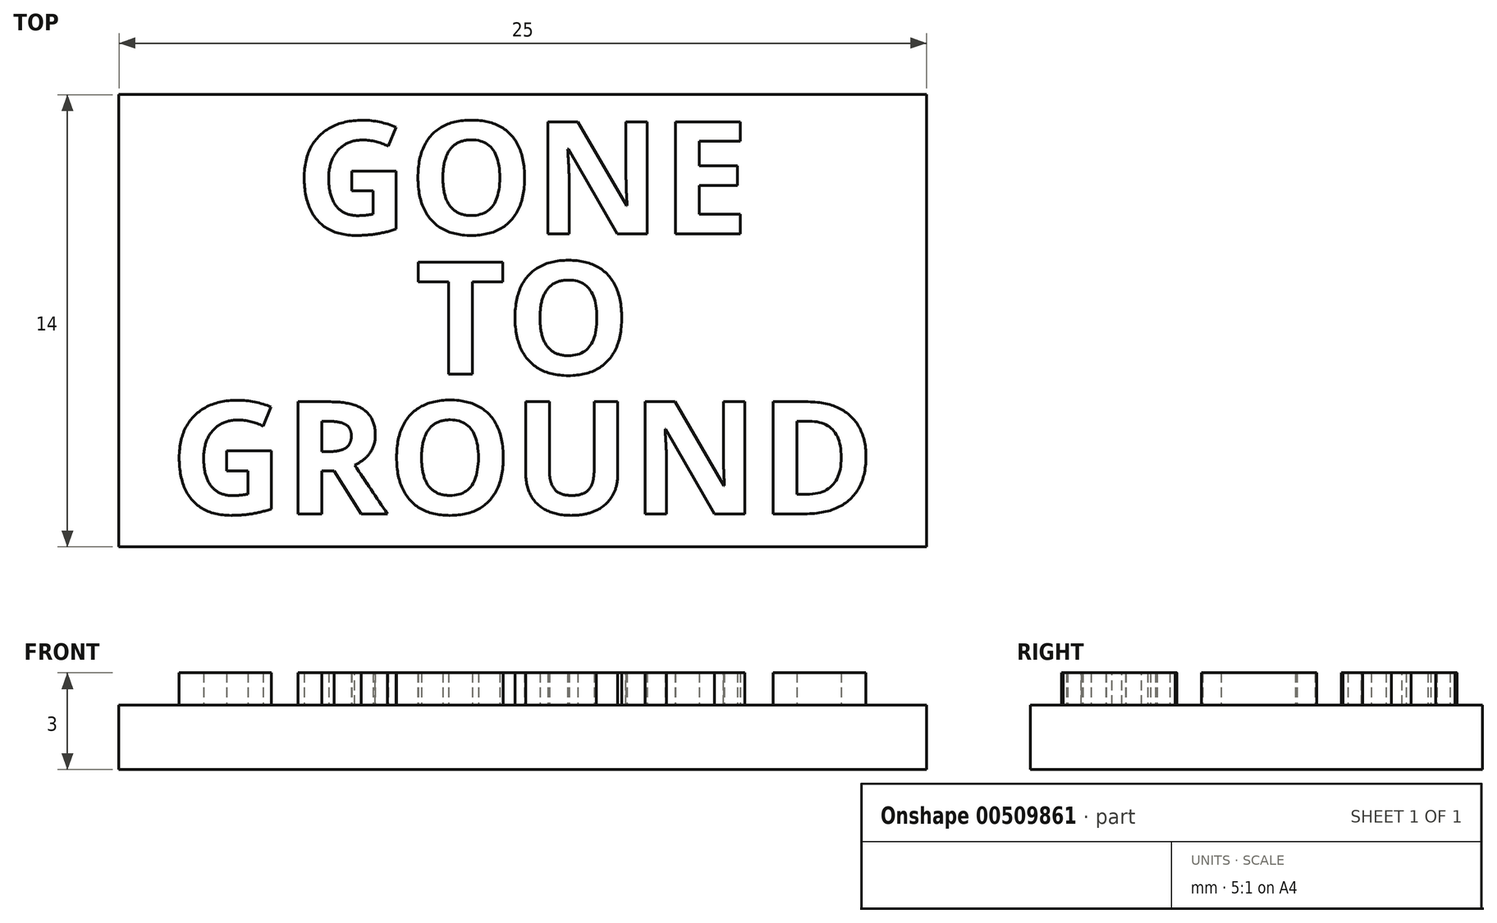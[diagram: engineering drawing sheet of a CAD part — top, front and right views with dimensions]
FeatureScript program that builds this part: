
annotation { "Feature Type Name" : "Feature", "Feature Type Description" : "" }
export const myFeature = defineFeature(function(context is Context, id is Id, definition is map)
    precondition{}
    {
        {
            var Q0;
            Q0=qCreatedBy(makeId("Top.planeOp"),FACE);
            var sketch = newSketch(context, id + "F0", { "sketchPlane" : qUnion([Q0])});
            skLineSegment(sketch, "E0.bottom", {"start": v(20.45, 63.88) * mm, "end": v(45.45, 63.88) * mm});
            skLineSegment(sketch, "E0.top", {"start": v(20.45, 49.88) * mm, "end": v(45.45, 49.88) * mm});
            skLineSegment(sketch, "E0.left", {"start": v(20.45, 63.88) * mm, "end": v(20.45, 49.88) * mm});
            skLineSegment(sketch, "E0.right", {"start": v(45.45, 63.88) * mm, "end": v(45.45, 49.88) * mm});
            skSolve(sketch);
        }
        {
            var Q0;
            Q0=qSketchRegion(id+"F0",true);
            extrude(context, id + "F1", {"entities" : qUnion([Q0]), "depth" : 2 * mm, "offsetDistance" : 25 * mm});
        }
        {
            var Q0;
            Q0=makeQuery(id+"F1.opExtrude","CAP_FACE",FACE,{"disambiguationData":[OSD([sQuery(id+"F0.wireOp",EDGE,"E0.bottom"),sQuery(id+"F0.wireOp",EDGE,"E0.top"),sQuery(id+"F0.wireOp",EDGE,"E0.left"),sQuery(id+"F0.wireOp",EDGE,"E0.right")])],"isStart":false});
            var sketch = newSketch(context, id + "F2", { "sketchPlane" : qUnion([Q0])});
            skText(sketch, "E1", { "text": "GROUND", "fontName": "OpenSans-Bold.ttf"});
            skText(sketch, "E2", { "text": "GONE", "fontName": "OpenSans-Bold.ttf"});
            skText(sketch, "E3", { "text": "TO", "fontName": "OpenSans-Bold.ttf"});
            const initialGuessF2  = {"E1": [0.02203, 0.0509, 1, 0, 0.0035], "E2": [0.0259, 0.05957, 1, 0, 0.0035], "E3": [0.02961, 0.05523, 1, 0, 0.0035]};
            skSetInitialGuess(sketch, initialGuessF2);
            skSolve(sketch);
        }
        {
            var Q0;
            Q0 = qSketchRegion(id + "F2", true);
            extrude(context, id + "F3", {"entities" : qUnion([Q0]), "operationType" : NewBodyOperationType.ADD, "depth" : 1 * mm, "offsetDistance" : 25 * mm});
        }
    });
